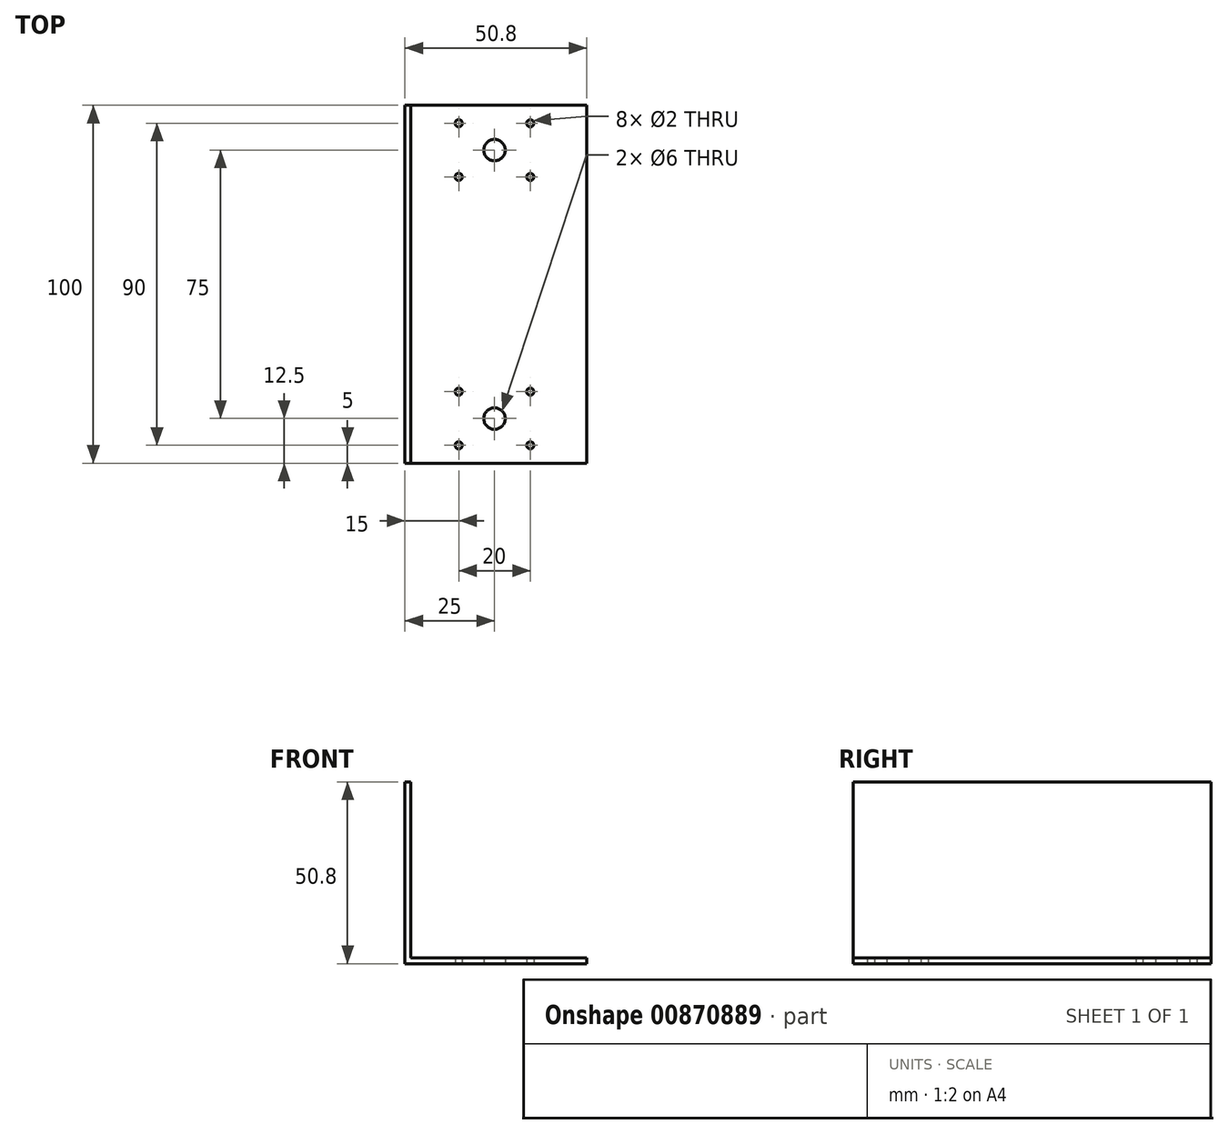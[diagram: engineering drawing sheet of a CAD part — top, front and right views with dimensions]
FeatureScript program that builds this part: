
annotation { "Feature Type Name" : "Feature", "Feature Type Description" : "" }
export const myFeature = defineFeature(function(context is Context, id is Id, definition is map)
    precondition{}
    {
        {
            var Q0;
            Q0=qCreatedBy(makeId("Front.planeOp"),FACE);
            var sketch = newSketch(context, id + "F0", { "sketchPlane" : qUnion([Q0])});
            skLineSegment(sketch, "E0", {"start": v(0, 0) * mm, "end": v(0, 50.8) * mm});
            skLineSegment(sketch, "E1", {"start": v(0, 50.8) * mm, "end": v(1.59, 50.8) * mm});
            skLineSegment(sketch, "E2", {"start": v(1.59, 50.8) * mm, "end": v(1.6, 1.59) * mm});
            skLineSegment(sketch, "E3", {"start": v(1.6, 1.59) * mm, "end": v(50.8, 1.6) * mm});
            skLineSegment(sketch, "E4", {"start": v(50.8, 1.6) * mm, "end": v(50.8, 0) * mm});
            skLineSegment(sketch, "E5", {"start": v(50.8, 0) * mm, "end": v(0, 0) * mm});
            skSolve(sketch);
        }
        {
            var Q0;
            Q0=qSketchRegion(id+"F0",true);
            extrude(context, id + "F1", {"entities" : qUnion([Q0]), "depth" : 100 * mm, "offsetDistance" : 25 * mm});
        }
        {
            var Q0;
            Q0=qCreatedBy(makeId("Top.planeOp"),FACE);
            var sketch = newSketch(context, id + "F2", { "sketchPlane" : qUnion([Q0])});
            skCircle(sketch, "E6", {"center": v(15, -5) * mm, "radius": 1 * mm});
            skCircle(sketch, "E7", {"center": v(35, -5) * mm, "radius": 1 * mm});
            skCircle(sketch, "E8", {"center": v(15, -20) * mm, "radius": 1 * mm});
            skCircle(sketch, "E9", {"center": v(35, -20) * mm, "radius": 1 * mm});
            skPoint(sketch, "E10", {"position": v(35, -80) * mm});
            skPoint(sketch, "E11", {"position": v(35, -95) * mm});
            skPoint(sketch, "E12", {"position": v(15, -80) * mm});
            skPoint(sketch, "E13", {"position": v(15, -95) * mm});
            skCircle(sketch, "E14", {"center": v(35, -80) * mm, "radius": 1 * mm});
            skCircle(sketch, "E15", {"center": v(15, -80) * mm, "radius": 1 * mm});
            skCircle(sketch, "E16", {"center": v(35, -95) * mm, "radius": 1 * mm});
            skCircle(sketch, "E17", {"center": v(15, -95) * mm, "radius": 1 * mm});
            skPoint(sketch, "E18", {"position": v(25, -12.5) * mm});
            skPoint(sketch, "E19", {"position": v(25, -87.5) * mm});
            skCircle(sketch, "E20", {"center": v(25, -87.5) * mm, "radius": 3 * mm});
            skCircle(sketch, "E21", {"center": v(25, -12.5) * mm, "radius": 3 * mm});
            skSolve(sketch);
        }
        {
            var Q0;
            Q0 = qSketchRegion(id + "F2", true);
            extrude(context, id + "F3", {"entities" : qUnion([Q0]), "operationType" : NewBodyOperationType.REMOVE, "endBound" : BoundingType.THROUGH_ALL, "depth" : 25 * mm, "offsetDistance" : 25 * mm});
        }
    });
